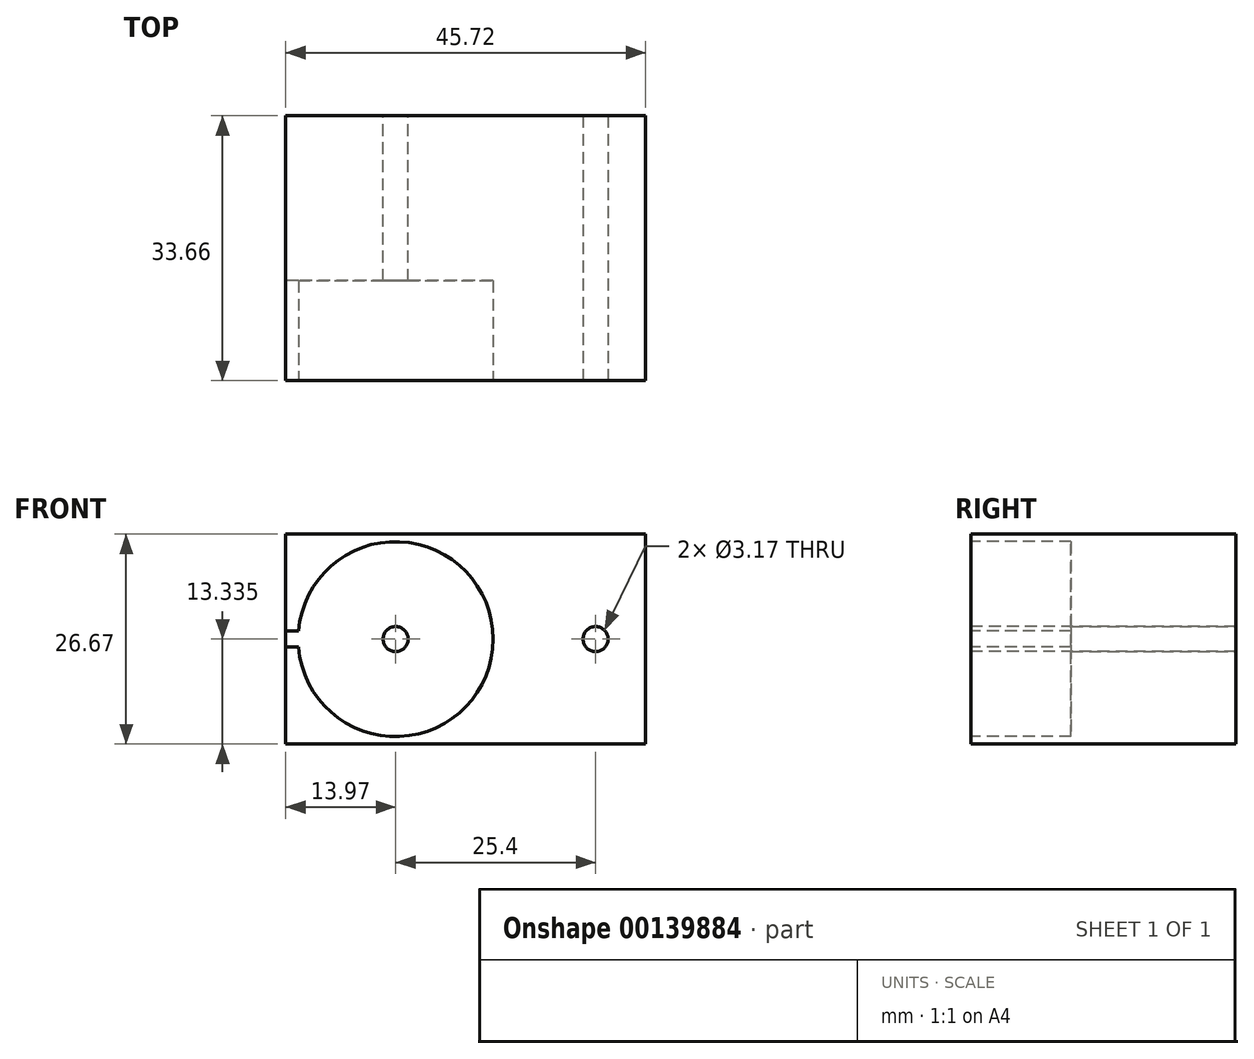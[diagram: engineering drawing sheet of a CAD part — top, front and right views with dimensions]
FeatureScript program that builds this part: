
annotation { "Feature Type Name" : "Feature", "Feature Type Description" : "" }
export const myFeature = defineFeature(function(context is Context, id is Id, definition is map)
    precondition{}
    {
        {
            var Q0;
            Q0=qCreatedBy(makeId("Front.planeOp"),FACE);
            var sketch = newSketch(context, id + "F0", { "sketchPlane" : qUnion([Q0])});
            skLineSegment(sketch, "E0.bottom", {"start": v(0, 0) * mm, "end": v(45.72, 0) * mm});
            skLineSegment(sketch, "E0.top", {"start": v(0, 26.67) * mm, "end": v(45.72, 26.67) * mm});
            skLineSegment(sketch, "E0.left", {"start": v(0, 0) * mm, "end": v(0, 26.67) * mm});
            skLineSegment(sketch, "E0.right", {"start": v(45.72, 0) * mm, "end": v(45.72, 26.67) * mm});
            skLineSegment(sketch, "E1", {"start": v(0, 13.33) * mm, "end": v(45.72, 13.33) * mm, "construction": true});
            skCircle(sketch, "E2", {"center": v(13.97, 13.33) * mm, "radius": 12.38 * mm});
            skCircle(sketch, "E3", {"center": v(39.37, 13.33) * mm, "radius": 1.59 * mm});
            skCircle(sketch, "E4", {"center": v(13.97, 13.33) * mm, "radius": 14.74 * mm});
            skCircle(sketch, "E5", {"center": v(39.37, 13.33) * mm, "radius": 3.35 * mm});
            skLineSegment(sketch, "E6", {"start": v(24.24, 23.91) * mm, "end": v(40.76, 16.39) * mm});
            skLineSegment(sketch, "E7", {"start": v(23.61, 2.19) * mm, "end": v(40.8, 10.3) * mm});
            skSolve(sketch);
        }
        {
            var Q0;
            Q0=makeQuery(id+"F0.imprint","IMPRINT",FACE,{"disambiguationData":[TD([[makeQuery(id+"F0.imprint","IMPRINT",EDGE,{"derivedFrom":sQuery(id+"F0.wireOp",EDGE,"E3")}),-1.0]])]});
            var Q1;
            {var subQ4=sQuery(id+"F0.wireOp",EDGE,"E0.right");Q1=makeQuery(id+"F0.imprint","IMPRINT",FACE,{"disambiguationData":[TD([[makeQuery(id+"F0.imprint","IMPRINT",EDGE,{"derivedFrom":subQ4}),1.0]])]});}
            var Q2;
            Q2=makeQuery(id+"F0.imprint","IMPRINT",FACE,{"disambiguationData":[TD([[makeQuery(id+"F0.imprint","IMPRINT",EDGE,{"derivedFrom":sQuery(id+"F0.wireOp",EDGE,"E2")}),-1.0]])]});
            var Q3;
            {var subQ0=sQuery(id+"F0.wireOp",EDGE,"E0.left");var subQ1=sQuery(id+"F0.wireOp",EDGE,"E0.top");var subQ2=makeQuery(id+"F0.imprint","INTERSECT",VERTEX,{"derivedFrom":[subQ1,subQ0]});Q3=makeQuery(id+"F0.imprint","IMPRINT",FACE,{"disambiguationData":[TD([[makeQuery(id+"F0.imprint","IMPRINT",EDGE,{"disambiguationData":[TD([[subQ2,-1.0]])],"derivedFrom":subQ1}),-1.0]])]});}
            var Q4;
            {var subQ0=sQuery(id+"F0.wireOp",EDGE,"E0.left");var subQ1=sQuery(id+"F0.wireOp",EDGE,"E0.bottom");var subQ2=makeQuery(id+"F0.imprint","INTERSECT",VERTEX,{"derivedFrom":[subQ1,subQ0]});Q4=makeQuery(id+"F0.imprint","IMPRINT",FACE,{"disambiguationData":[TD([[makeQuery(id+"F0.imprint","IMPRINT",EDGE,{"disambiguationData":[TD([[subQ2,-1.0]])],"derivedFrom":subQ1}),1.0]])]});}
            var Q5;
            {var subQ0=sQuery(id+"F0.wireOp",EDGE,"E6");Q5=makeQuery(id+"F0.imprint","IMPRINT",FACE,{"disambiguationData":[TD([[makeQuery(id+"F0.imprint","IMPRINT",EDGE,{"derivedFrom":subQ0}),-1.0]])]});}
            extrude(context, id + "F1", {"entities" : qUnion([Q0, Q1, Q2, Q3, Q4, Q5]), "oppositeDirection" : true, "depth" : 33.65 * mm});
        }
        {
            var Q0;
            Q0=makeQuery(id+"F1.opExtrude","CAP_FACE",FACE,{"disambiguationData":[OSD([sQuery(id+"F0.wireOp",EDGE,"E0.bottom"),sQuery(id+"F0.wireOp",EDGE,"E0.top"),sQuery(id+"F0.wireOp",EDGE,"E0.left"),sQuery(id+"F0.wireOp",EDGE,"E0.right"),sQuery(id+"F0.wireOp",EDGE,"E2"),sQuery(id+"F0.wireOp",EDGE,"E3")])],"isStart":true});
            var sketch = newSketch(context, id + "F2", { "sketchPlane" : qUnion([Q0])});
            skPoint(sketch, "E8", {"position": v(0, 13.33) * mm});
            skLineSegment(sketch, "E9.bottom", {"start": v(3, 14.35) * mm, "end": v(-3, 14.35) * mm});
            skLineSegment(sketch, "E9.top", {"start": v(3, 12.32) * mm, "end": v(-3, 12.32) * mm});
            skLineSegment(sketch, "E9.left", {"start": v(3, 14.35) * mm, "end": v(3, 12.32) * mm});
            skLineSegment(sketch, "E9.right", {"start": v(-3, 14.35) * mm, "end": v(-3, 12.32) * mm});
            skSolve(sketch);
        }
        {
            var Q0;
            Q0 = qSketchRegion(id + "F2", true);
            extrude(context, id + "F3", {"entities" : qUnion([Q0]), "operationType" : NewBodyOperationType.REMOVE, "oppositeDirection" : true, "depth" : 12.7 * mm});
        }
        {
            var Q0;
            Q0=makeQuery(id+"F1.opExtrude","CAP_FACE",FACE,{"disambiguationData":[OSD([sQuery(id+"F0.wireOp",EDGE,"E0.bottom"),sQuery(id+"F0.wireOp",EDGE,"E0.top"),sQuery(id+"F0.wireOp",EDGE,"E0.left"),sQuery(id+"F0.wireOp",EDGE,"E0.right"),sQuery(id+"F0.wireOp",EDGE,"E2"),sQuery(id+"F0.wireOp",EDGE,"E3")])],"isStart":false});
            var sketch = newSketch(context, id + "F4", { "sketchPlane" : qUnion([Q0])});
            skCircle(sketch, "E10", {"center": v(-13.97, 13.33) * mm, "radius": 1.59 * mm});
            skSolve(sketch);
        }
        {
            var Q0;
            Q0=makeQuery(id+"F4.imprint","IMPRINT",FACE,{"disambiguationData":[TD([[makeQuery(id+"F4.imprint","IMPRINT",EDGE,{"derivedFrom":sQuery(id+"F4.wireOp",EDGE,"E10")}),-1.0]])]});
            extrude(context, id + "F5", {"entities" : qUnion([Q0]), "operationType" : NewBodyOperationType.ADD, "oppositeDirection" : true, "depth" : 20.95 * mm});
        }
    });
